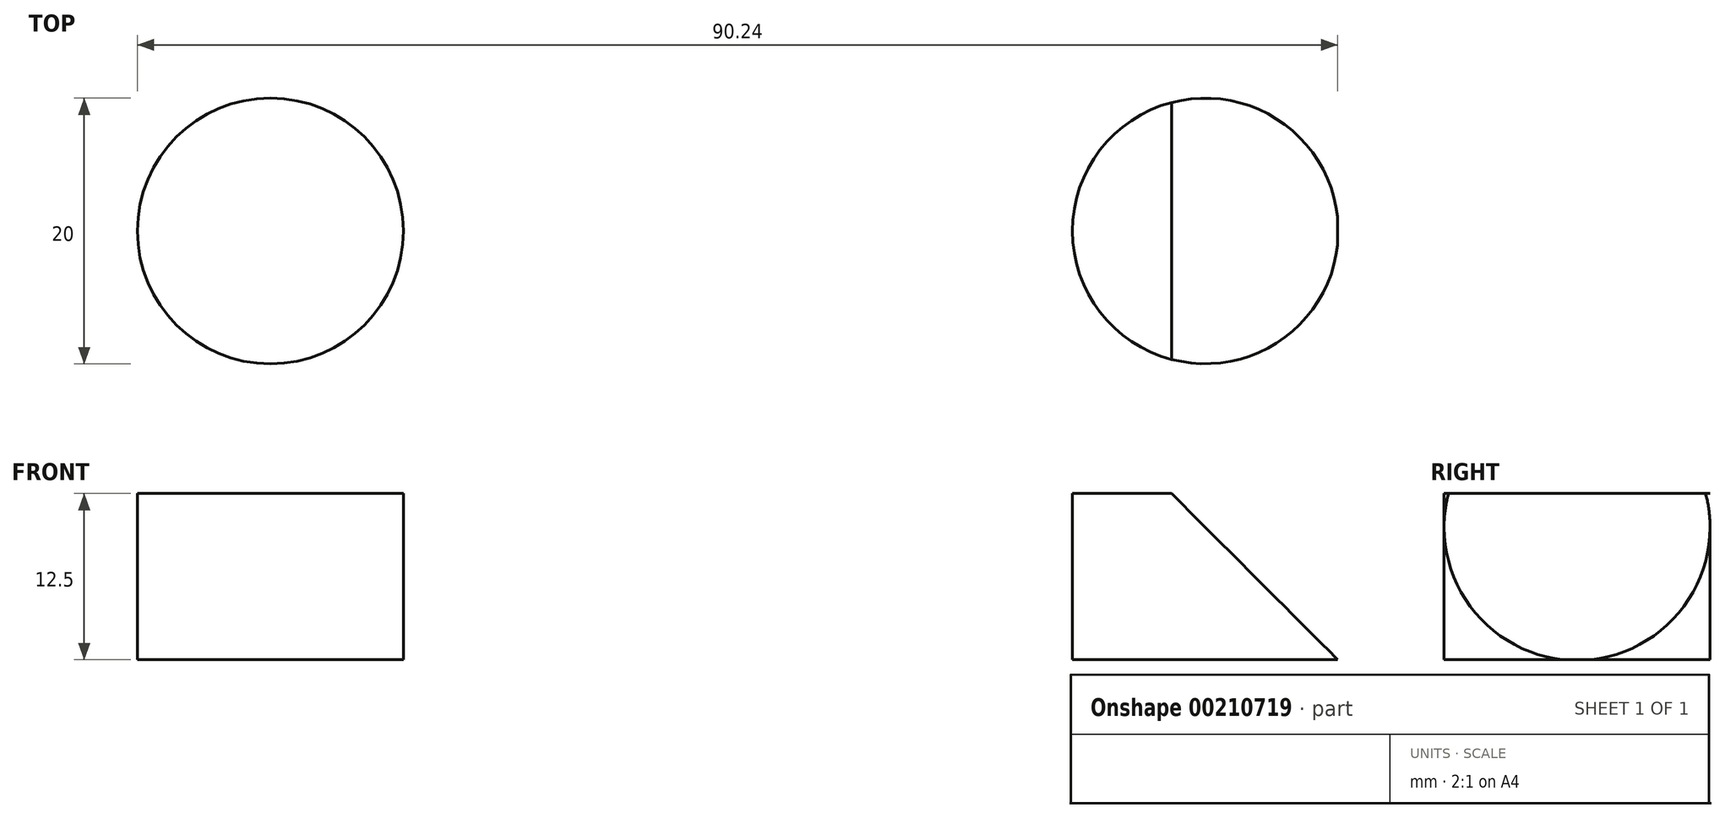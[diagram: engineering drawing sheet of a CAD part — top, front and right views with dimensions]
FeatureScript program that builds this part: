
annotation { "Feature Type Name" : "Feature", "Feature Type Description" : "" }
export const myFeature = defineFeature(function(context is Context, id is Id, definition is map)
    precondition{}
    {
        {
            var Q0;
            Q0=qCreatedBy(makeId("Top.planeOp"),FACE);
            var sketch = newSketch(context, id + "F0", { "sketchPlane" : qUnion([Q0])});
            skCircle(sketch, "E0", {"center": v(0, 0) * mm, "radius": 10 * mm});
            skCircle(sketch, "E1", {"center": v(-70.3, 0) * mm, "radius": 10 * mm});
            skLineSegment(sketch, "E2", {"start": v(-10, 0) * mm, "end": v(10, 0) * mm});
            skLineSegment(sketch, "E3", {"start": v(-60.3, 0) * mm, "end": v(-80.3, 0) * mm});
            skSolve(sketch);
        }
        {
            var Q0;
            Q0 = qSketchRegion(id + "F0", true);
            extrude(context, id + "F1", {"entities" : qUnion([Q0]), "depth" : 12.5 * mm});
        }
        {
            var Q0;
            Q0=qCreatedBy(makeId("Front.planeOp"),FACE);
            var sketch = newSketch(context, id + "F2", { "sketchPlane" : qUnion([Q0])});
            skLineSegment(sketch, "E4", {"start": v(-10.3, 20.25) * mm, "end": v(9.94, 0) * mm});
            skLineSegment(sketch, "E5", {"start": v(9.94, 20.25) * mm, "end": v(-10.3, 20.25) * mm});
            skLineSegment(sketch, "E6", {"start": v(9.94, 0) * mm, "end": v(13.9, 0) * mm});
            skLineSegment(sketch, "E7", {"start": v(13.9, 0) * mm, "end": v(13.9, 20.25) * mm});
            skLineSegment(sketch, "E8", {"start": v(9.94, 20.25) * mm, "end": v(13.9, 20.25) * mm});
            skPoint(sketch, "E9.end.orphan", {"position": v(9.94, 0) * mm});
            skSolve(sketch);
        }
        {
            var Q0;
            Q0 = qSketchRegion(id + "F2", true);
            extrude(context, id + "F3", {"entities" : qUnion([Q0]), "operationType" : NewBodyOperationType.REMOVE, "depth" : 50 * mm, "symmetric" : true});
        }
    });
